FCSTD DOCUMENT  (FreeCAD 0.16R6353 (Git))
Label: SteelSection_L
License: All rights reserved
LicenseURL: http://de.wikipedia.org/wiki/Alle_Rechte_vorbehalten
objects: Sketcher::SketchObject×1
note: 1 computed .brp shape members not serialized (recipe doc carries the construction recipe); baked Part::Feature solids carry a one-line shape summary decoded from their .brp

FEATURE [Sketcher::SketchObject] Sketch  label="xsec"
  sketch-geometry (11):
    g0: LineSegment StartX=0 StartY=0 StartZ=0 EndX=75 EndY=0 EndZ=0
    g1: LineSegment StartX=75 StartY=0 StartZ=0 EndX=75 EndY=6 EndZ=0
    g2: LineSegment StartX=74 StartY=7 StartZ=0 EndX=8 EndY=7 EndZ=0
    g3: LineSegment StartX=7 StartY=8 StartZ=0 EndX=7 EndY=99 EndZ=0
    g4: LineSegment StartX=6 StartY=100 StartZ=0 EndX=0 EndY=100 EndZ=0
    g5: LineSegment StartX=0 StartY=100 StartZ=0 EndX=0 EndY=0 EndZ=0
    g6: ArcOfCircle CenterX=6 CenterY=99 CenterZ=0 NormalX=0 NormalY=0 NormalZ=1 Radius=1 StartAngle=0 EndAngle=1.5708
    g7: ArcOfCircle CenterX=8 CenterY=8 CenterZ=0 NormalX=0 NormalY=0 NormalZ=1 Radius=1 StartAngle=3.14159 EndAngle=4.71239
    g8: ArcOfCircle CenterX=74 CenterY=6 CenterZ=0 NormalX=0 NormalY=0 NormalZ=1 Radius=1 StartAngle=0 EndAngle=1.5708
    g9: LineSegment [constr] StartX=7 StartY=8 StartZ=0 EndX=0 EndY=8 EndZ=0
    g10: LineSegment [constr] StartX=8 StartY=7 StartZ=0 EndX=8 EndY=0 EndZ=0
  constraints (29):
    c: Coincident(g-1,g0)
    c: Horizontal(g0)
    c: Coincident(g0,g1)
    c: Vertical(g1)
    c: Horizontal(g2)
    c: Horizontal(g4)
    c: Coincident(g4,g5)
    c: Coincident(g5,g0)
    c: Vertical(g5)
    c: Vertical(g3)
    c: Tangent(g4,g6) = -1.5708
    c: Tangent(g3,g6) = -1.5708
    c: Tangent(g3,g7) = 1.5708
    c: Tangent(g2,g7) = 1.5708
    c: Tangent(g2,g8) = -1.5708
    c: Tangent(g1,g8) = -1.5708
    c: DistanceX(g0) = 75  'b'
    c: Radius(g6) = 1  'r2'
    c: Coincident(g9,g3)  'Constraint19'
    c: PointOnObject(g9,g5)
    c: Horizontal(g9)
    c: PointOnObject(g10,g0)
    c: Vertical(g10)
    c: Equal(g9,g10)
    c: Coincident(g10,g2)
    c: Radius(g7) = 1  'r1'
    c: Equal(g8,g6)
    c: Distance(g9) = 7  't'
    c: Distance(g5) = 100  'h'
